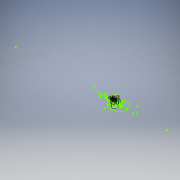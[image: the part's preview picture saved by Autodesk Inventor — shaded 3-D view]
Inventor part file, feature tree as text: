
AUTODESK INVENTOR PART (.ipt)
format: ipt  version: 2018 (Build 220112000, 112)  size: 351,744 bytes
history: native  units: mm
features: sketch x53, plane x13, revolve x1
ambient origin geometry x8: Origin, YZ Plane, XZ Plane, XY Plane, X Axis, Y Axis, Z Axis, Center Point
bodies: Solid1 (feature_tree)
feature tree (67):
  sketch  "Sketch1"  dims[d10=50.0mm d21=40.0mm]
  sketch  "Sketch2"  dims[d22=38.0mm]
  sketch  "Sketch3"  dims[d65=46.0mm]
  sketch  "Sketch4"  dims[d66=48.3mm]
  sketch  "Sketch5"  dims[d87=30.0mm]
  sketch  "Sketch7"  dims[d166=180.0deg]
  sketch  "Sketch8"
  sketch  "Sketch9"
  sketch  "Sketch10"
  sketch  "Sketch11"
  sketch  "Sketch12"
  sketch  "Sketch13"
  sketch  "Sketch16"
  sketch  "Sketch18"
  sketch  "Sketch19"
  sketch  "Sketch20"
  sketch  "Sketch21"
  sketch  "Sketch22"
  sketch  "Sketch23"
  sketch  "Sketch24"
  sketch  "Sketch25"
  sketch  "Sketch31"
  sketch  "Sketch32"
  sketch  "Sketch34"
  sketch  "Sketch35"
  plane  "Work Plane16"
  sketch  "Sketch36"
  sketch  "Sketch37"
  sketch  "Sketch38"
  sketch  "Sketch39"
  sketch  "Sketch40"
  sketch  "Sketch41"
  plane  "Work Plane13"
  sketch  "Sketch43"
  plane  "Work Plane14"
  sketch  "Sketch45"
  sketch  "Sketch47"
  sketch  "Sketch48"
  sketch  "Sketch49"
  sketch  "Sketch50"
  sketch  "Sketch52"
  sketch  "Sketch53"
  sketch  "Sketch55"
  plane  "Work Plane5"
  sketch  "Sketch56"
  plane  "Work Plane3"
  plane  "Work Plane6"
  sketch  "Sketch57"
  plane  "Work Plane7"
  sketch  "Sketch58"
  plane  "Work Plane8"
  sketch  "Sketch59"
  sketch  "Sketch60"
  plane  "Work Plane9"
  sketch  "Sketch61"
  plane  "Work Plane10"
  sketch  "Sketch62"
  plane  "Work Plane12"
  sketch  "Sketch65"
  plane  "Work Plane11"
  sketch  "Sketch67"
  plane  "Work Plane15"
  sketch  "Sketch68"
  sketch  "Sketch69"
  sketch  "Sketch70"
  revolve  "Revolution4"  [1 undecoded]
  sketch  "Sketch71"
note: 1 required parameter value undecoded (feature->parameter linkage not recoverable at this tier; creation-order binding heuristic only, values carry confidence <= 0.55)
